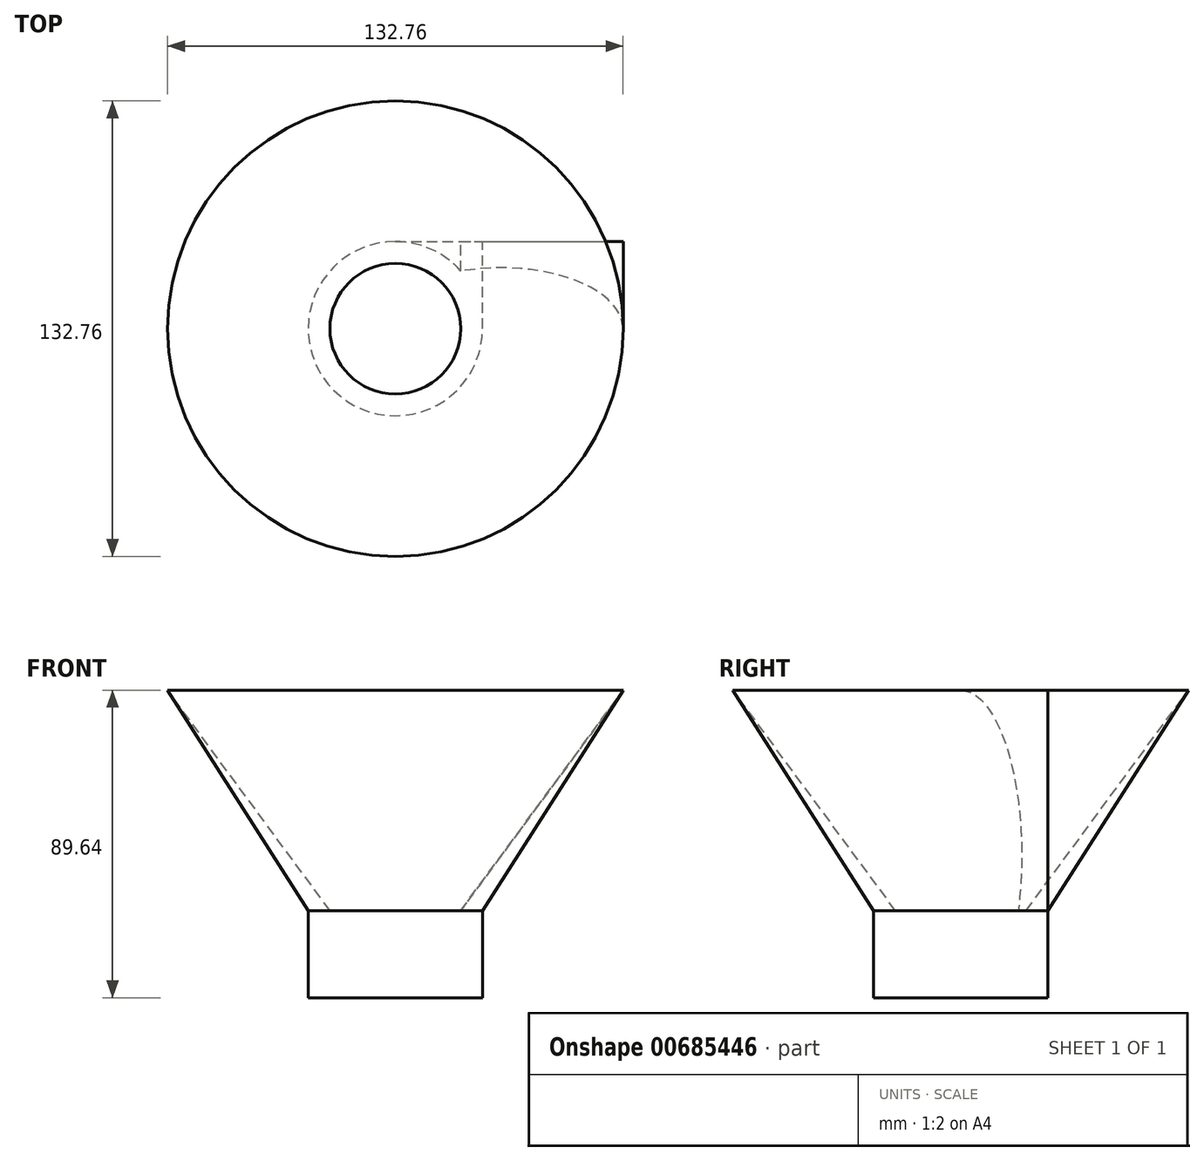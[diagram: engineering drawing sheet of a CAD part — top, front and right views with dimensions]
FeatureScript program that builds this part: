
annotation { "Feature Type Name" : "Feature", "Feature Type Description" : "" }
export const myFeature = defineFeature(function(context is Context, id is Id, definition is map)
    precondition{}
    {
        {
            var Q0;
            Q0=qCreatedBy(makeId("Front.planeOp"),FACE);
            var sketch = newSketch(context, id + "F0", { "sketchPlane" : qUnion([Q0])});
            skLineSegment(sketch, "E0", {"start": v(-60.65, 0) * mm, "end": v(-60.65, -25.4) * mm});
            skLineSegment(sketch, "E1", {"start": v(-60.65, -25.4) * mm, "end": v(-35.25, -25.4) * mm});
            skLineSegment(sketch, "E2", {"start": v(-35.25, -25.4) * mm, "end": v(-35.25, 0) * mm});
            skLineSegment(sketch, "E3", {"start": v(-60.65, 0) * mm, "end": v(-41.6, 0) * mm});
            skLineSegment(sketch, "E4", {"start": v(-35.25, 0) * mm, "end": v(5.73, 64.24) * mm});
            skLineSegment(sketch, "E5", {"start": v(-41.6, 0) * mm, "end": v(5.73, 64.24) * mm});
            skSolve(sketch);
        }
        {
            var Q0;
            Q0=makeQuery(id+"F0.imprint","IMPRINT",FACE,{"disambiguationData":[TD([[makeQuery(id+"F0.imprint","IMPRINT",EDGE,{"derivedFrom":sQuery(id+"F0.wireOp",EDGE,"E0")}),1.0]])]});
            extrude(context, id + "F1", {"entities" : qUnion([Q0]), "depth" : 25.4 * mm, "offsetDistance" : 25.4 * mm});
        }
        {
            var Q0;
            Q0=makeQuery(id+"F1.opExtrude","CAP_FACE",FACE,{"disambiguationData":[OSD([sQuery(id+"F0.wireOp",EDGE,"E0"),sQuery(id+"F0.wireOp",EDGE,"E1"),sQuery(id+"F0.wireOp",EDGE,"E2"),sQuery(id+"F0.wireOp",EDGE,"E3"),sQuery(id+"F0.wireOp",EDGE,"E4"),sQuery(id+"F0.wireOp",EDGE,"E5")])],"isStart":false});
            var Q1;
            Q1=makeQuery(id+"F1.opExtrude","CAP_EDGE",EDGE,{"disambiguationData":[OSD([sQuery(id+"F0.wireOp",EDGE,"E0")])],"isStart":false});
            revolve(context, id + "F2", {"operationType" : NewBodyOperationType.ADD, "surfaceOperationType" : NewSurfaceOperationType.NEW, "entities" : qUnion([Q0]), "axis" : qUnion([Q1]), "revolveType" : RevolveType.FULL});
        }
    });
